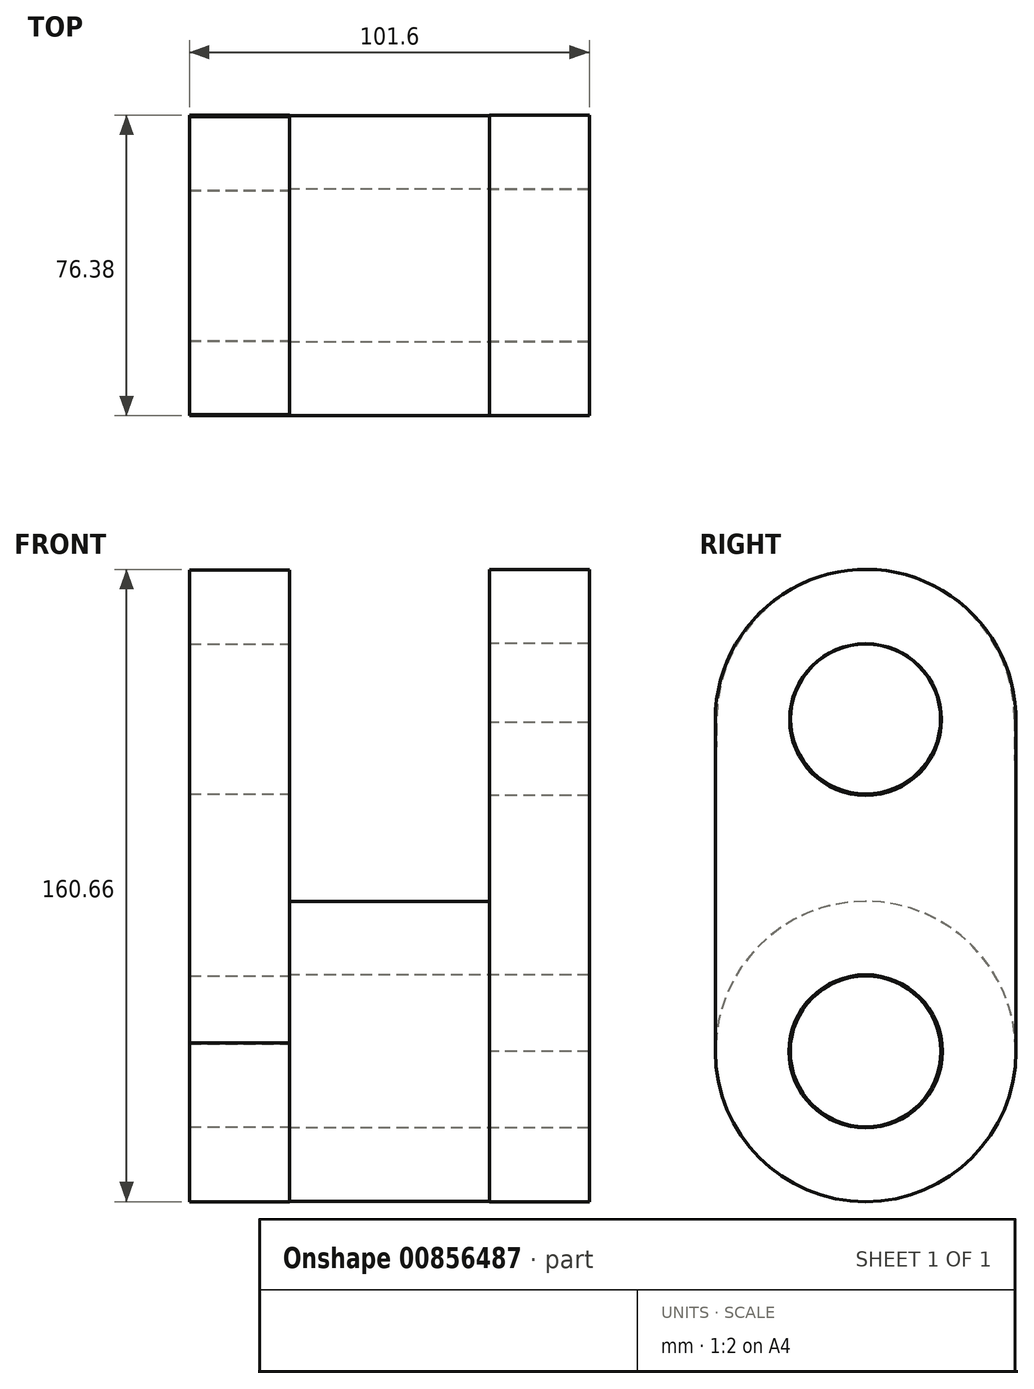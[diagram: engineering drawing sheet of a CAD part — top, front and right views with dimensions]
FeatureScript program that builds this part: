
annotation { "Feature Type Name" : "Feature", "Feature Type Description" : "" }
export const myFeature = defineFeature(function(context is Context, id is Id, definition is map)
    precondition{}
    {
        {
            var Q0;
            Q0=qCreatedBy(makeId("Right.planeOp"),FACE);
            var sketch = newSketch(context, id + "F0", { "sketchPlane" : qUnion([Q0])});
            skArc(sketch, "E0", {"start": v(-38.2, 0) * mm, "mid": v(0.34, -38.19) * mm, "end": v(38.18, 0.68) * mm});
            skCircle(sketch, "E1", {"center": v(0, 0) * mm, "radius": 19.46 * mm});
            skLineSegment(sketch, "E2.left", {"start": v(-38.2, 0) * mm, "end": v(-38.2, 0) * mm});
            skLineSegment(sketch, "E2.right", {"start": v(38.2, 0) * mm, "end": v(38.2, 0) * mm});
            skLineSegment(sketch, "E3.left", {"start": v(-38.2, 0) * mm, "end": v(-38.2, 84.27) * mm});
            skLineSegment(sketch, "E3.right", {"start": v(38.18, 0) * mm, "end": v(38.18, 84.27) * mm});
            skLineSegment(sketch, "E4.trimOffspring", {"start": v(38.18, 0) * mm, "end": v(38.2, 0) * mm});
            skArc(sketch, "E5", {"start": v(38.18, 83.59) * mm, "mid": v(0.34, 122.46) * mm, "end": v(-38.2, 84.27) * mm});
            skCircle(sketch, "E6", {"center": v(0, 84.27) * mm, "radius": 19.28 * mm});
            skSolve(sketch);
        }
        {
            var Q0;
            Q0=makeQuery(id+"F0.imprint","IMPRINT",FACE,{"disambiguationData":[TD([[makeQuery(id+"F0.imprint","IMPRINT",EDGE,{"derivedFrom":sQuery(id+"F0.wireOp",EDGE,"E1")}),-1.0]])]});
            extrude(context, id + "F1", {"entities" : qUnion([Q0]), "depth" : 25.4 * mm, "offsetDistance" : 25.4 * mm});
        }
        {
            var Q0;
            Q0=makeQuery(id+"F1.opExtrude","CAP_FACE",FACE,{"disambiguationData":[OSD([sQuery(id+"F0.wireOp",EDGE,"E0"),sQuery(id+"F0.wireOp",EDGE,"E1"),sQuery(id+"F0.wireOp",EDGE,"E3.left"),sQuery(id+"F0.wireOp",EDGE,"E3.right"),sQuery(id+"F0.wireOp",EDGE,"E4.trimOffspring"),sQuery(id+"F0.wireOp",EDGE,"E5"),sQuery(id+"F0.wireOp",EDGE,"E6")])],"isStart":true});
            var sketch = newSketch(context, id + "F2", { "sketchPlane" : qUnion([Q0])});
            skCircle(sketch, "E7", {"center": v(0, 0) * mm, "radius": 38.13 * mm});
            skSolve(sketch);
        }
        {
            var Q0;
            Q0=makeQuery(id+"F2.imprint","IMPRINT",FACE,{"disambiguationData":[TD([[makeQuery(id+"F2.imprint","IMPRINT",EDGE,{"derivedFrom":sQuery(id+"F2.wireOp",EDGE,"E7")}),1.0]])]});
            extrude(context, id + "F3", {"entities" : qUnion([Q0]), "operationType" : NewBodyOperationType.ADD, "depth" : 50.8 * mm, "offsetDistance" : 25.4 * mm});
        }
        {
            var Q0;
            Q0=makeQuery(id+"F3.opExtrude","CAP_FACE",FACE,{"disambiguationData":[OSD([sQuery(id+"F0.wireOp",EDGE,"E1"),sQuery(id+"F2.wireOp",EDGE,"E7")])],"isStart":false});
            var sketch = newSketch(context, id + "F4", { "sketchPlane" : qUnion([Q0])});
            skArc(sketch, "E8", {"start": v(-38.13, 1.95) * mm, "mid": v(0.07, -38.18) * mm, "end": v(38.12, 2.1) * mm});
            skLineSegment(sketch, "E9", {"start": v(-38.13, 0) * mm, "end": v(-38.13, 1.95) * mm});
            skLineSegment(sketch, "E10", {"start": v(38.13, 1.9) * mm, "end": v(38.13, 0) * mm});
            skLineSegment(sketch, "E11", {"start": v(-38.13, 1.95) * mm, "end": v(-38.13, 0) * mm});
            skArc(sketch, "E12", {"start": v(37.82, 84.43) * mm, "mid": v(0, 122.25) * mm, "end": v(-37.82, 84.43) * mm});
            skLineSegment(sketch, "E13", {"start": v(-37.82, 84.43) * mm, "end": v(-38.13, 1.95) * mm});
            skLineSegment(sketch, "E14", {"start": v(38.13, 0) * mm, "end": v(37.82, 84.43) * mm});
            skCircle(sketch, "E15", {"center": v(0, 84.43) * mm, "radius": 19.05 * mm});
            skCircle(sketch, "E16", {"center": v(0, 0) * mm, "radius": 19.15 * mm});
            skSolve(sketch);
        }
        {
            var Q0;
            Q0 = qSketchRegion(id + "F4", true);
            extrude(context, id + "F5", {"entities" : qUnion([Q0]), "operationType" : NewBodyOperationType.ADD, "depth" : 25.4 * mm, "offsetDistance" : 25.4 * mm});
        }
    });
